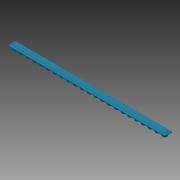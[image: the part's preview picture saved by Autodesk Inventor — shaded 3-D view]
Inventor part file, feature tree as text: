
AUTODESK INVENTOR PART (.ipt)
format: ipt  version: 2015 (Build 190159000, 159)  size: 431,616 bytes
history: native  units: mm
features: extrude x6, sketch x6, pattern_linear x4
ambient origin geometry x8: Origin, YZ Plane, XZ Plane, XY Plane, X Axis, Y Axis, Z Axis, Center Point
bodies: 实体1 (feature_tree)
feature tree (16):
  extrude  "拉伸1"  Depth=55.0mm
  extrude  "拉伸2"  Depth=10.0mm
  extrude  "拉伸3"  Depth=5.0mm
  extrude  "拉伸4"  Depth=1155.0mm TaperAngle=0.0deg
  extrude  "拉伸5"  Depth=5.0mm
  pattern_linear  "矩形阵列1"  Spacing1=5.0mm  [1 undecoded]
  extrude  "拉伸6"  TaperAngle=135.0deg  [1 undecoded]
  pattern_linear  "矩形阵列3"  Spacing1=55.0mm  [1 undecoded]
  pattern_linear  "矩形阵列4"  Spacing1=27.5mm  [1 undecoded]
  pattern_linear  "矩形阵列5"  Spacing1=27.5mm  [1 undecoded]
  sketch  "草图1"  dims[d0=1155.0mm d1=55.0mm]
  sketch  "草图2"  dims[d2=10.0mm d3=0.0mm d4=10.0mm]
  sketch  "草图3"  dims[d5=10.0mm d6=5.0mm]
  sketch  "草图4"  dims[d7=5.0mm d8=1155.0mm d9=0.0mm]
  sketch  "草图5"  dims[d10=10.0mm d11=5.0mm]
  sketch  "草图6"  dims[d12=10.0mm d13=5.0mm d14=135.0deg d15=55.0mm d16=0.0mm d17=27.5mm d18=27.5mm d19=3.75mm d20=20.0mm d21=0.0mm d22=1.5mm d23=1.5mm d24=1.5mm d25=1.5mm d26=10.0mm d27=0.0mm d28=230.0mm d30=50.0mm d31=4.0mm d32=4.0mm d33=5.0mm d34=5.0mm d35=5.0mm d36=5.0mm d37=5.0mm d38=0.0mm d42=20.0mm d44=197.5mm d45=60.0mm d47=150.0mm d48=20.0mm d50=1145.0mm]
note: 5 required parameter values undecoded (feature->parameter linkage not recoverable at this tier; creation-order binding heuristic only, values carry confidence <= 0.55)
